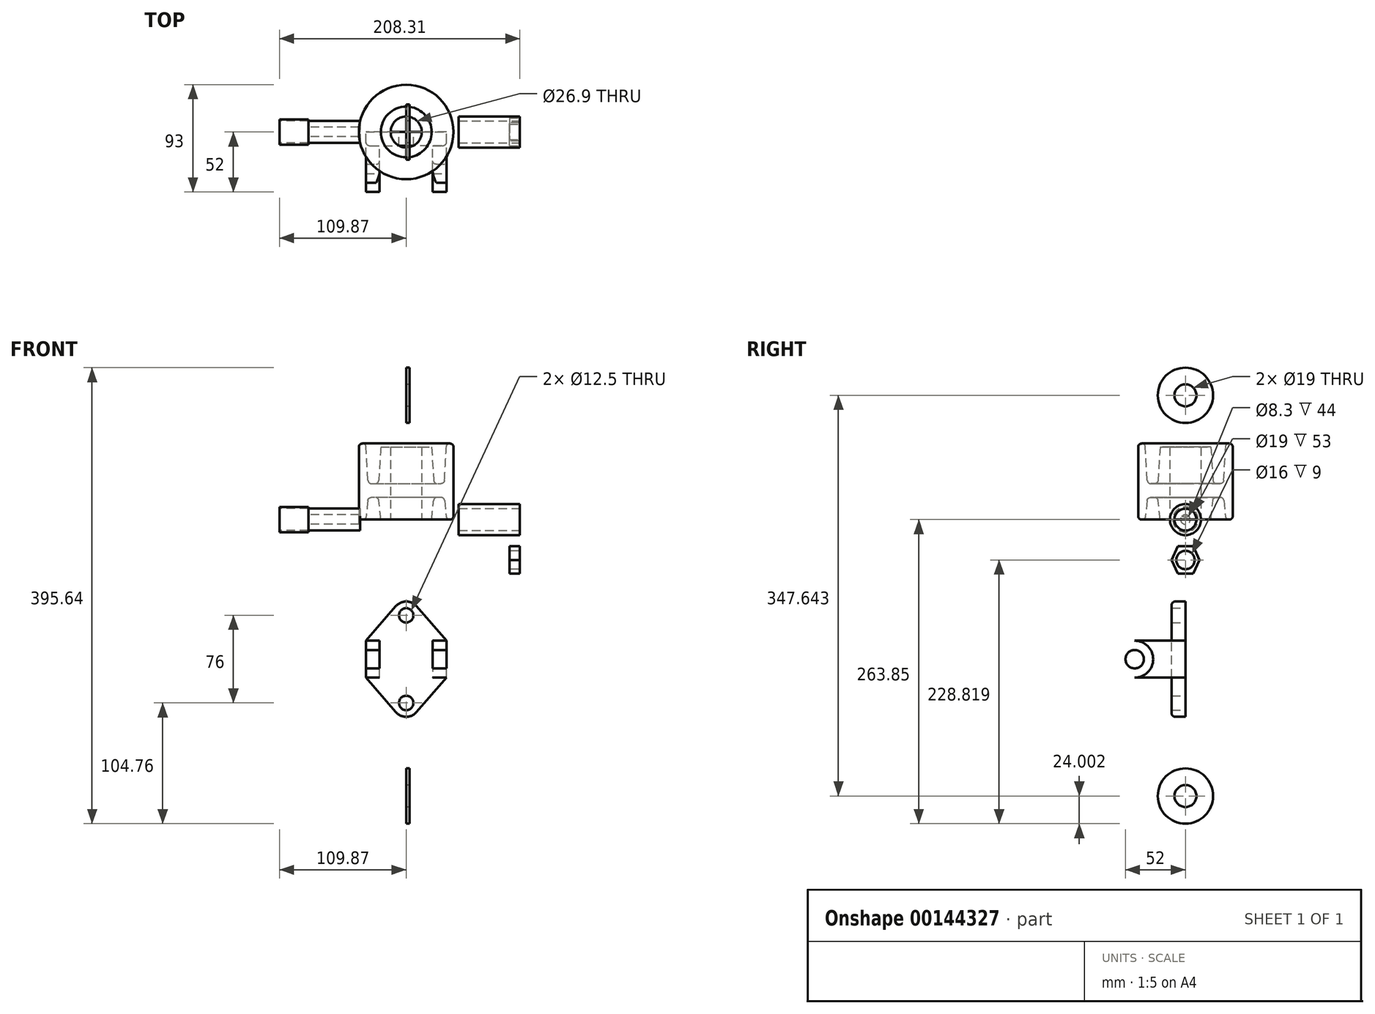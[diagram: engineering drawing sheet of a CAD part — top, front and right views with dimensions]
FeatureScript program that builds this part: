
annotation { "Feature Type Name" : "Feature", "Feature Type Description" : "" }
export const myFeature = defineFeature(function(context is Context, id is Id, definition is map)
    precondition{}
    {
        {
            var Q0;
            Q0=qCreatedBy(makeId("Front.planeOp"),FACE);
            var sketch = newSketch(context, id + "F0", { "sketchPlane" : qUnion([Q0])});
            skLineSegment(sketch, "E0", {"start": v(-13.45, 0) * mm, "end": v(-13.45, 63) * mm});
            skLineSegment(sketch, "E1", {"start": v(-13.45, 63) * mm, "end": v(-22, 63) * mm});
            skLineSegment(sketch, "E2", {"start": v(-22, 63) * mm, "end": v(-24, 31.2) * mm});
            skLineSegment(sketch, "E3", {"start": v(-24, 31.2) * mm, "end": v(-33, 31.2) * mm});
            skLineSegment(sketch, "E4", {"start": v(-33, 31.2) * mm, "end": v(-35, 66) * mm});
            skLineSegment(sketch, "E5", {"start": v(-35, 66) * mm, "end": v(-41, 66) * mm});
            skLineSegment(sketch, "E6", {"start": v(-41, 66) * mm, "end": v(-41, 0) * mm});
            skLineSegment(sketch, "E7", {"start": v(-41, 0) * mm, "end": v(-35, 0) * mm});
            skLineSegment(sketch, "E8", {"start": v(-35, 0) * mm, "end": v(-33, 19.2) * mm});
            skLineSegment(sketch, "E9", {"start": v(-33, 19.2) * mm, "end": v(-24, 19.2) * mm});
            skLineSegment(sketch, "E10", {"start": v(-24, 19.2) * mm, "end": v(-22, 0) * mm});
            skLineSegment(sketch, "E11", {"start": v(-22, 0) * mm, "end": v(-13.45, 0) * mm});
            skLineSegment(sketch, "E12", {"start": v(0, 0) * mm, "end": v(0, 72.33) * mm, "construction": true});
            skSolve(sketch);
        }
        {
            var Q0;
            Q0 = qSketchRegion(id + "F0", true);
            var Q1;
            Q1=sQuery(id+"F0.wireOp",EDGE,"E12");
            revolve(context, id + "F1", {"entities" : qUnion([Q0]), "axis" : qUnion([Q1]), "revolveType" : RevolveType.FULL});
        }
        {
            var Q0;
            Q0=makeQuery(id+"F1.opRevolve","SWEPT_EDGE",EDGE,{"disambiguationData":[OSD([sQuery(id+"F0.wireOp",EDGE,"E5"),sQuery(id+"F0.wireOp",EDGE,"E6")])]});
            var Q1;
            Q1=makeQuery(id+"F1.opRevolve","SWEPT_EDGE",EDGE,{"disambiguationData":[OSD([sQuery(id+"F0.wireOp",EDGE,"E4"),sQuery(id+"F0.wireOp",EDGE,"E5")])]});
            var Q2;
            Q2=makeQuery(id+"F1.opRevolve","SWEPT_EDGE",EDGE,{"disambiguationData":[OSD([sQuery(id+"F0.wireOp",EDGE,"E2"),sQuery(id+"F0.wireOp",EDGE,"E3")])]});
            var Q3;
            Q3=makeQuery(id+"F1.opRevolve","SWEPT_FACE",FACE,{"disambiguationData":[OSD([sQuery(id+"F0.wireOp",EDGE,"E3")])]});
            var Q4;
            Q4=makeQuery(id+"F1.opRevolve","SWEPT_EDGE",EDGE,{"disambiguationData":[OSD([sQuery(id+"F0.wireOp",EDGE,"E6"),sQuery(id+"F0.wireOp",EDGE,"E7")])]});
            var Q5;
            Q5=makeQuery(id+"F1.opRevolve","SWEPT_EDGE",EDGE,{"disambiguationData":[OSD([sQuery(id+"F0.wireOp",EDGE,"E7"),sQuery(id+"F0.wireOp",EDGE,"E8")])]});
            fillet(context, id + "F2", {"entities" : qUnion([Q0, Q1, Q2, Q3, Q4, Q5]), "radius" : 3 * mm, "tangentPropagation" : true, "allowEdgeOverflow" : false});
        }
        {
            var Q0;
            Q0=makeQuery(id+"F1.opRevolve","SWEPT_EDGE",EDGE,{"disambiguationData":[OSD([sQuery(id+"F0.wireOp",EDGE,"E8"),sQuery(id+"F0.wireOp",EDGE,"E9")])]});
            var Q1;
            Q1=makeQuery(id+"F1.opRevolve","SWEPT_EDGE",EDGE,{"disambiguationData":[OSD([sQuery(id+"F0.wireOp",EDGE,"E9"),sQuery(id+"F0.wireOp",EDGE,"E10")])]});
            fillet(context, id + "F3", {"entities" : qUnion([Q0, Q1]), "radius" : 3 * mm, "tangentPropagation" : true, "allowEdgeOverflow" : false});
        }
        {
            var Q0;
            Q0=qCreatedBy(makeId("Front.planeOp"),FACE);
            var sketch = newSketch(context, id + "F4", { "sketchPlane" : qUnion([Q0])});
            skLineSegment(sketch, "E13", {"start": v(-35, -105.09) * mm, "end": v(-9.06, -75.22) * mm});
            skLineSegment(sketch, "E14", {"start": v(9.06, -75.22) * mm, "end": v(35, -105.09) * mm});
            skLineSegment(sketch, "E15", {"start": v(35, -105.09) * mm, "end": v(35, -137.09) * mm});
            skLineSegment(sketch, "E16", {"start": v(35, -137.09) * mm, "end": v(9.06, -166.96) * mm});
            skLineSegment(sketch, "E17", {"start": v(-9.06, -166.96) * mm, "end": v(-35, -137.09) * mm});
            skLineSegment(sketch, "E18", {"start": v(-35, -137.09) * mm, "end": v(-35, -105.09) * mm});
            skArc(sketch, "E19", {"start": v(-9.06, -75.22) * mm, "mid": v(0, -71.09) * mm, "end": v(9.06, -75.22) * mm});
            skArc(sketch, "E20", {"start": v(-9.06, -166.96) * mm, "mid": v(0, -171.09) * mm, "end": v(9.06, -166.96) * mm});
            skCircle(sketch, "E21", {"center": v(0, -83.09) * mm, "radius": 6.25 * mm});
            skCircle(sketch, "E22", {"center": v(0, -159.09) * mm, "radius": 6.25 * mm});
            skLineSegment(sketch, "E23", {"start": v(0, 0) * mm, "end": v(0, -228.96) * mm, "construction": true});
            skSolve(sketch);
        }
        {
            var Q0;
            Q0 = qSketchRegion(id + "F4", true);
            extrude(context, id + "F5", {"entities" : qUnion([Q0]), "depth" : 12 * mm});
        }
        {
            var Q0;
            Q0=makeQuery(id+"F5.opExtrude","CAP_FACE",FACE,{"disambiguationData":[OSD([sQuery(id+"F4.wireOp",EDGE,"E13"),sQuery(id+"F4.wireOp",EDGE,"E14"),sQuery(id+"F4.wireOp",EDGE,"E15"),sQuery(id+"F4.wireOp",EDGE,"E16"),sQuery(id+"F4.wireOp",EDGE,"E17"),sQuery(id+"F4.wireOp",EDGE,"E18"),sQuery(id+"F4.wireOp",EDGE,"E19"),sQuery(id+"F4.wireOp",EDGE,"E20"),sQuery(id+"F4.wireOp",EDGE,"E21"),sQuery(id+"F4.wireOp",EDGE,"E22")])],"isStart":false});
            var sketch = newSketch(context, id + "F6", { "sketchPlane" : qUnion([Q0])});
            skLineSegment(sketch, "E24.0", {"start": v(35, -105.09) * mm, "end": v(35, -137.09) * mm});
            skLineSegment(sketch, "E25.0", {"start": v(-35, -137.09) * mm, "end": v(-35, -105.09) * mm});
            skLineSegment(sketch, "E26", {"start": v(-35, -105.09) * mm, "end": v(-23, -105.09) * mm});
            skLineSegment(sketch, "E27", {"start": v(-23, -105.09) * mm, "end": v(-23, -137.09) * mm});
            skLineSegment(sketch, "E28", {"start": v(-23, -137.09) * mm, "end": v(-35, -137.09) * mm});
            skLineSegment(sketch, "E29", {"start": v(35, -137.09) * mm, "end": v(23, -137.09) * mm});
            skLineSegment(sketch, "E30", {"start": v(23, -137.09) * mm, "end": v(23, -105.09) * mm});
            skLineSegment(sketch, "E31", {"start": v(23, -105.09) * mm, "end": v(35, -105.09) * mm});
            skSolve(sketch);
        }
        {
            var Q0;
            Q0 = qSketchRegion(id + "F6", true);
            extrude(context, id + "F7", {"entities" : qUnion([Q0]), "operationType" : NewBodyOperationType.ADD, "depth" : 48 * mm});
        }
        {
            var Q0;
            Q0=makeQuery(id+"F7.boolean.opBoolean","MERGE",FACE,{"derivedFrom":[makeQuery(id+"F5.opExtrude","SWEPT_FACE",FACE,{"disambiguationData":[OSD([sQuery(id+"F4.wireOp",EDGE,"E15")])]}),makeQuery(id+"F7.opExtrude","SWEPT_FACE",FACE,{"disambiguationData":[OSD([sQuery(id+"F6.wireOp",EDGE,"E24.0")])]})]});
            var sketch = newSketch(context, id + "F8", { "sketchPlane" : qUnion([Q0])});
            skLineSegment(sketch, "E32.0", {"start": v(-60, -137.09) * mm, "end": v(-12, -137.09) * mm});
            skLineSegment(sketch, "E33.0", {"start": v(-60, -105.09) * mm, "end": v(-12, -105.09) * mm});
            skArc(sketch, "E34", {"start": v(-44, -105.09) * mm, "mid": v(-60, -121.09) * mm, "end": v(-44, -137.09) * mm});
            skLineSegment(sketch, "E35.0", {"start": v(-60, -105.09) * mm, "end": v(-60, -137.09) * mm});
            skCircle(sketch, "E36", {"center": v(-44, -121.09) * mm, "radius": 8 * mm});
            skSolve(sketch);
        }
        {
            var Q0;
            Q0 = qSketchRegion(id + "F8", true);
            extrude(context, id + "F9", {"entities" : qUnion([Q0]), "operationType" : NewBodyOperationType.REMOVE, "oppositeDirection" : true, "depth" : 172.56 * mm});
        }
        {
            var Q0;
            Q0=qCreatedBy(makeId("Right.planeOp"),FACE);
            var sketch = newSketch(context, id + "F10", { "sketchPlane" : qUnion([Q0])});
            skCircle(sketch, "E37", {"center": v(0, 107.8) * mm, "radius": 9.5 * mm});
            skCircle(sketch, "E38", {"center": v(0, 107.8) * mm, "radius": 24 * mm});
            skSolve(sketch);
        }
        {
            var Q0;
            Q0 = qSketchRegion(id + "F10", true);
            extrude(context, id + "F11", {"entities" : qUnion([Q0]), "depth" : 3 * mm});
        }
        {
            var Q0;
            {var subQ0=sQuery(id+"F8.wireOp",EDGE,"E34");var subQ1=makeQuery(id+"F8.imprint","INTERSECT",VERTEX,{"derivedFrom":[subQ0,sQuery(id+"F8.wireOp",EDGE,"E35.0")]});Q0=makeQuery(id+"F9.boolean.opBoolean","INTERSECT",EDGE,{"derivedFrom":[makeQuery(id+"F7.opExtrude","SWEPT_FACE",FACE,{"disambiguationData":[OSD([sQuery(id+"F6.wireOp",EDGE,"E27")])]}),makeQuery(id+"F9.opExtrude","SWEPT_FACE",FACE,{"disambiguationData":[OSD([subQ0]),TDD([makeQuery(id+"F8.imprint","IMPRINT",EDGE,{"disambiguationData":[TD([[subQ1,-1.0]])],"derivedFrom":subQ0})])]}),makeQuery(id+"F9.opExtrude","SWEPT_FACE",FACE,{"disambiguationData":[OSD([subQ0]),TDD([makeQuery(id+"F8.imprint","IMPRINT",EDGE,{"disambiguationData":[TD([[subQ1,1.0]])],"derivedFrom":subQ0})])]})]});}
            var Q1;
            Q1=makeQuery(id+"F7.opExtrude","CAP_EDGE",EDGE,{"disambiguationData":[OSD([sQuery(id+"F6.wireOp",EDGE,"E27")])],"isStart":true});
            var Q2;
            {var subQ0=sQuery(id+"F8.wireOp",EDGE,"E34");var subQ1=makeQuery(id+"F8.imprint","INTERSECT",VERTEX,{"derivedFrom":[subQ0,sQuery(id+"F8.wireOp",EDGE,"E35.0")]});Q2=makeQuery(id+"F9.boolean.opBoolean","INTERSECT",EDGE,{"derivedFrom":[makeQuery(id+"F7.opExtrude","SWEPT_FACE",FACE,{"disambiguationData":[OSD([sQuery(id+"F6.wireOp",EDGE,"E30")])]}),makeQuery(id+"F9.opExtrude","SWEPT_FACE",FACE,{"disambiguationData":[OSD([subQ0]),TDD([makeQuery(id+"F8.imprint","IMPRINT",EDGE,{"disambiguationData":[TD([[subQ1,-1.0]])],"derivedFrom":subQ0})])]}),makeQuery(id+"F9.opExtrude","SWEPT_FACE",FACE,{"disambiguationData":[OSD([subQ0]),TDD([makeQuery(id+"F8.imprint","IMPRINT",EDGE,{"disambiguationData":[TD([[subQ1,1.0]])],"derivedFrom":subQ0})])]})]});}
            var Q3;
            Q3=makeQuery(id+"F7.opExtrude","CAP_EDGE",EDGE,{"disambiguationData":[OSD([sQuery(id+"F6.wireOp",EDGE,"E30")])],"isStart":true});
            fillet(context, id + "F12", {"entities" : qUnion([Q0, Q1, Q2, Q3]), "radius" : 3 * mm, "tangentPropagation" : true, "allowEdgeOverflow" : false});
        }
        {
            var Q0;
            Q0=makeQuery(id+"F5.opExtrude","CAP_EDGE",EDGE,{"disambiguationData":[OSD([sQuery(id+"F4.wireOp",EDGE,"E13")])],"isStart":false});
            var Q1;
            Q1=makeQuery(id+"F5.opExtrude","CAP_EDGE",EDGE,{"disambiguationData":[OSD([sQuery(id+"F4.wireOp",EDGE,"E17")])],"isStart":false});
            fillet(context, id + "F13", {"entities" : qUnion([Q0, Q1]), "radius" : 3 * mm, "tangentPropagation" : true, "allowEdgeOverflow" : false});
        }
        {
            var Q0;
            Q0=qCreatedBy(makeId("Front.planeOp"),FACE);
            var sketch = newSketch(context, id + "F14", { "sketchPlane" : qUnion([Q0])});
            skLineSegment(sketch, "E39", {"start": v(-109.87, 0) * mm, "end": v(98.44, 0) * mm, "construction": true});
            skSolve(sketch);
        }
        {
            var Q0;
            Q0=sQuery(id+"F14.wireOp",VERTEX,"E39.end");
            var Q1;
            Q1=qCreatedBy(makeId("Right.planeOp"),FACE);
            cPlane(context, id + "F15", {"entities" : qUnion([Q0, Q1]), "cplaneType" : CPlaneType.PLANE_POINT, "offset" : 25 * mm, "width" : 150 * mm, "height" : 150 * mm});
        }
        {
            var Q0;
            Q0=qCreatedBy(id+"F15.planeOp",FACE);
            var sketch = newSketch(context, id + "F16", { "sketchPlane" : qUnion([Q0])});
            skCircle(sketch, "E40", {"center": v(0, 0) * mm, "radius": 9.5 * mm});
            skCircle(sketch, "E41", {"center": v(0, 0) * mm, "radius": 13.45 * mm});
            skSolve(sketch);
        }
        {
            var Q0;
            Q0 = qSketchRegion(id + "F16", true);
            extrude(context, id + "F17", {"entities" : qUnion([Q0]), "oppositeDirection" : true, "depth" : 53 * mm});
        }
        {
            var Q0;
            Q0=sQuery(id+"F14.wireOp",VERTEX,"E39.start");
            var Q1;
            Q1=qCreatedBy(makeId("Right.planeOp"),FACE);
            cPlane(context, id + "F18", {"entities" : qUnion([Q0, Q1]), "cplaneType" : CPlaneType.PLANE_POINT, "offset" : 25 * mm, "width" : 150 * mm, "height" : 150 * mm});
        }
        {
            var Q0;
            Q0=qCreatedBy(id+"F18.planeOp",FACE);
            var sketch = newSketch(context, id + "F19", { "sketchPlane" : qUnion([Q0])});
            skCircle(sketch, "E42", {"center": v(0, 0) * mm, "radius": 11 * mm});
            skSolve(sketch);
        }
        {
            var Q0;
            Q0 = qSketchRegion(id + "F19", true);
            extrude(context, id + "F20", {"entities" : qUnion([Q0]), "depth" : 25 * mm});
        }
        {
            var Q0;
            Q0=qCreatedBy(id+"F18.planeOp",FACE);
            var sketch = newSketch(context, id + "F21", { "sketchPlane" : qUnion([Q0])});
            skCircle(sketch, "E43", {"center": v(0, 0) * mm, "radius": 9.5 * mm});
            skSolve(sketch);
        }
        {
            var Q0;
            Q0 = qSketchRegion(id + "F21", true);
            extrude(context, id + "F22", {"entities" : qUnion([Q0]), "depth" : 70 * mm});
        }
        {
            var Q0;
            Q0=makeQuery(id+"F20.opExtrude","CAP_FACE",FACE,{"disambiguationData":[OSD([sQuery(id+"F19.wireOp",EDGE,"E42")])],"isStart":false});
            var sketch = newSketch(context, id + "F23", { "sketchPlane" : qUnion([Q0])});
            skCircle(sketch, "E44", {"center": v(0, 0) * mm, "radius": 4.15 * mm});
            skSolve(sketch);
        }
        {
            var Q0;
            Q0 = qSketchRegion(id + "F23", true);
            extrude(context, id + "F24", {"entities" : qUnion([Q0]), "operationType" : NewBodyOperationType.REMOVE, "depth" : 44 * mm});
        }
        {
            var Q0;
            Q0=qCreatedBy(id+"F15.planeOp",FACE);
            var sketch = newSketch(context, id + "F25", { "sketchPlane" : qUnion([Q0])});
            skLineSegment(sketch, "E45", {"start": v(0, -23.03) * mm, "end": v(0, -47.03) * mm, "construction": true});
            skLineSegment(sketch, "E46", {"start": v(-12, -35.03) * mm, "end": v(12, -35.03) * mm, "construction": true});
            skPoint(sketch, "E46.startSnap0", {"position": v(0, -35.03) * mm});
            skLineSegment(sketch, "E47", {"start": v(-12, -35.03) * mm, "end": v(-6.58, -23.03) * mm});
            skLineSegment(sketch, "E48", {"start": v(-6.58, -23.03) * mm, "end": v(6.58, -23.03) * mm});
            skLineSegment(sketch, "E49", {"start": v(6.58, -23.03) * mm, "end": v(12, -35.03) * mm});
            skLineSegment(sketch, "E50", {"start": v(12, -35.03) * mm, "end": v(6.58, -47.03) * mm});
            skLineSegment(sketch, "E51", {"start": v(6.58, -47.03) * mm, "end": v(-6.58, -47.03) * mm});
            skLineSegment(sketch, "E52", {"start": v(-6.58, -47.03) * mm, "end": v(-12, -35.03) * mm});
            skSolve(sketch);
        }
        {
            var Q0;
            Q0 = qSketchRegion(id + "F25", true);
            extrude(context, id + "F26", {"entities" : qUnion([Q0]), "oppositeDirection" : true, "depth" : 9 * mm});
        }
        {
            var Q0;
            Q0=makeQuery(id+"F26.opExtrude","CAP_FACE",FACE,{"disambiguationData":[OSD([sQuery(id+"F25.wireOp",EDGE,"E47"),sQuery(id+"F25.wireOp",EDGE,"E48"),sQuery(id+"F25.wireOp",EDGE,"E49"),sQuery(id+"F25.wireOp",EDGE,"E50"),sQuery(id+"F25.wireOp",EDGE,"E51"),sQuery(id+"F25.wireOp",EDGE,"E52")])],"isStart":true});
            var sketch = newSketch(context, id + "F27", { "sketchPlane" : qUnion([Q0])});
            skCircle(sketch, "E53", {"center": v(0, -35.03) * mm, "radius": 8 * mm});
            skPoint(sketch, "E53.centerSnap0", {"position": v(0, -23.03) * mm});
            skSolve(sketch);
        }
        {
            var Q0;
            Q0 = qSketchRegion(id + "F27", true);
            extrude(context, id + "F28", {"entities" : qUnion([Q0]), "operationType" : NewBodyOperationType.REMOVE, "depth" : 10 * mm, "hasSecondDirection" : true, "secondDirectionOppositeDirection" : true, "secondDirectionDepth" : 10 * mm});
        }
        {
            var Q0;
            Q0=qCreatedBy(makeId("Front.planeOp"),FACE);
            var sketch = newSketch(context, id + "F29", { "sketchPlane" : qUnion([Q0])});
            skLineSegment(sketch, "E54", {"start": v(0, 178.4) * mm, "end": v(0, -284.12) * mm, "construction": true});
            skSolve(sketch);
        }
        {
            var Q0;
            Q0=sQuery(id+"F29.wireOp",VERTEX,"E54.end");
            var Q1;
            Q1=qCreatedBy(makeId("Right.planeOp"),FACE);
            cPlane(context, id + "F30", {"entities" : qUnion([Q0, Q1]), "cplaneType" : CPlaneType.PLANE_POINT, "offset" : 25 * mm, "width" : 150 * mm, "height" : 150 * mm});
        }
        {
            var Q0;
            Q0=qCreatedBy(id+"F30.planeOp",FACE);
            var sketch = newSketch(context, id + "F31", { "sketchPlane" : qUnion([Q0])});
            skCircle(sketch, "E55", {"center": v(0, -239.85) * mm, "radius": 24 * mm});
            skCircle(sketch, "E56", {"center": v(0, -239.85) * mm, "radius": 9.5 * mm});
            skSolve(sketch);
        }
        {
            var Q0;
            Q0 = qSketchRegion(id + "F31", true);
            extrude(context, id + "F32", {"entities" : qUnion([Q0]), "depth" : 3 * mm});
        }
    });
